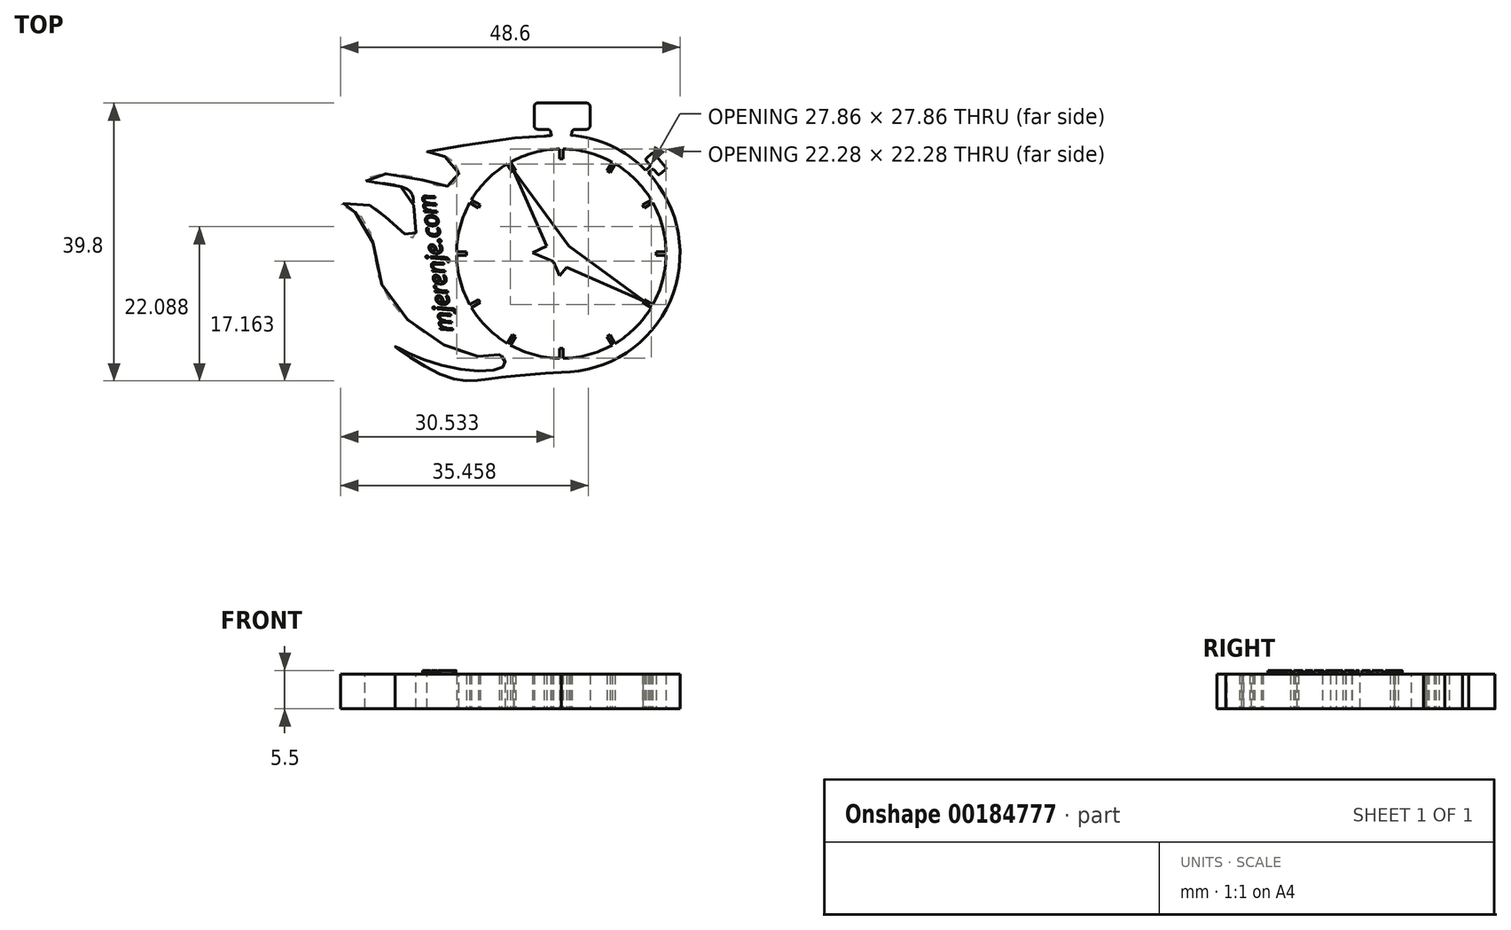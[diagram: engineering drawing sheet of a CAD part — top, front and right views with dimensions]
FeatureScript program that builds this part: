
annotation { "Feature Type Name" : "Feature", "Feature Type Description" : "" }
export const myFeature = defineFeature(function(context is Context, id is Id, definition is map)
    precondition{}
    {
        {
            var Q0;
            Q0=qCreatedBy(makeId("Top.planeOp"),FACE);
            var sketch = newSketch(context, id + "F0", { "sketchPlane" : qUnion([Q0])});
            skArc(sketch, "E0", {"start": v(-0.25, 15) * mm, "mid": v(-3.88, 14.49) * mm, "end": v(-7.28, 13.11) * mm});
            skArc(sketch, "E1.0", {"start": v(-1.33, 16.95) * mm, "mid": v(-1.9, 16.9) * mm, "end": v(-2.47, 16.82) * mm});
            skLineSegment(sketch, "E2.0", {"start": v(-0.25, 15) * mm, "end": v(-0.25, 13.57) * mm});
            skLineSegment(sketch, "E3.0", {"start": v(0.25, 15) * mm, "end": v(0.25, 13.57) * mm});
            skLineSegment(sketch, "E4", {"start": v(-0.25, 13.57) * mm, "end": v(0.25, 13.57) * mm});
            skLineSegment(sketch, "E5", {"start": v(-27.27, 0) * mm, "end": v(32.4, 0) * mm, "construction": true});
            skPoint(sketch, "E6", {"position": v(0, 13.57) * mm});
            skLineSegment(sketch, "E7.1.0", {"start": v(7.28, 13.12) * mm, "end": v(6.57, 11.87) * mm});
            skPoint(sketch, "E7.1.1", {"position": v(6.78, 11.75) * mm});
            skLineSegment(sketch, "E7.1.2", {"start": v(7.72, 12.87) * mm, "end": v(7, 11.62) * mm});
            skLineSegment(sketch, "E7.1.3", {"start": v(6.57, 11.87) * mm, "end": v(7, 11.62) * mm});
            skLineSegment(sketch, "E7.2.0", {"start": v(12.87, 7.72) * mm, "end": v(11.62, 7) * mm});
            skPoint(sketch, "E7.2.1", {"position": v(11.75, 6.78) * mm});
            skLineSegment(sketch, "E7.2.2", {"start": v(13.12, 7.28) * mm, "end": v(11.87, 6.57) * mm});
            skLineSegment(sketch, "E7.2.3", {"start": v(11.62, 7) * mm, "end": v(11.87, 6.57) * mm});
            skLineSegment(sketch, "E7.3.0", {"start": v(15, 0.25) * mm, "end": v(13.57, 0.25) * mm});
            skPoint(sketch, "E7.3.1", {"position": v(13.57, 0) * mm});
            skLineSegment(sketch, "E7.3.2", {"start": v(15, -0.25) * mm, "end": v(13.57, -0.25) * mm});
            skLineSegment(sketch, "E7.3.3", {"start": v(13.57, 0.25) * mm, "end": v(13.57, -0.25) * mm});
            skLineSegment(sketch, "E7.anchor1", {"start": v(0, 0) * mm, "end": v(0, 13.57) * mm, "construction": true});
            skLineSegment(sketch, "E7.anchor2", {"start": v(0, 0) * mm, "end": v(13.57, 0) * mm, "construction": true});
            skLineSegment(sketch, "E8.MirrorCS", {"start": v(-11.62, 7) * mm, "end": v(-11.87, 6.57) * mm});
            skLineSegment(sketch, "E9.MirrorCS", {"start": v(-13.57, 0.25) * mm, "end": v(-13.57, -0.25) * mm});
            skPoint(sketch, "E10.MirrorP", {"position": v(-13.57, 0) * mm});
            skPoint(sketch, "E11.MirrorP", {"position": v(-6.78, 11.75) * mm});
            skLineSegment(sketch, "E12.MirrorCS", {"start": v(-13.12, 7.28) * mm, "end": v(-11.87, 6.57) * mm});
            skLineSegment(sketch, "E13.MirrorCS", {"start": v(-15, 0.25) * mm, "end": v(-13.57, 0.25) * mm});
            skLineSegment(sketch, "E14.MirrorCS", {"start": v(-15, -0.25) * mm, "end": v(-13.57, -0.25) * mm});
            skPoint(sketch, "E15.MirrorP", {"position": v(-11.75, 6.78) * mm});
            skLineSegment(sketch, "E16.MirrorCS", {"start": v(-7.72, 12.87) * mm, "end": v(-7, 11.62) * mm});
            skLineSegment(sketch, "E17.MirrorCS", {"start": v(-12.87, 7.72) * mm, "end": v(-11.62, 7) * mm});
            skLineSegment(sketch, "E18.MirrorCS", {"start": v(-7.28, 13.12) * mm, "end": v(-6.57, 11.87) * mm});
            skLineSegment(sketch, "E19.MirrorCS", {"start": v(-6.57, 11.87) * mm, "end": v(-7, 11.62) * mm});
            skLineSegment(sketch, "E20.MirrorCS", {"start": v(-0.25, -13.57) * mm, "end": v(0.25, -13.57) * mm});
            skLineSegment(sketch, "E21.MirrorCS", {"start": v(6.57, -11.87) * mm, "end": v(7, -11.62) * mm});
            skLineSegment(sketch, "E22.MirrorCS", {"start": v(-11.62, -7) * mm, "end": v(-11.87, -6.57) * mm});
            skLineSegment(sketch, "E23.MirrorCS", {"start": v(-6.57, -11.87) * mm, "end": v(-7, -11.62) * mm});
            skLineSegment(sketch, "E24.MirrorCS", {"start": v(11.62, -7) * mm, "end": v(11.87, -6.57) * mm});
            skLineSegment(sketch, "E25.MirrorCS", {"start": v(-12.87, -7.72) * mm, "end": v(-11.62, -7) * mm});
            skLineSegment(sketch, "E26.MirrorCS", {"start": v(0.25, -15) * mm, "end": v(0.25, -13.57) * mm});
            skLineSegment(sketch, "E27.MirrorCS", {"start": v(-0.25, -15) * mm, "end": v(-0.25, -13.57) * mm});
            skLineSegment(sketch, "E28.MirrorCS", {"start": v(-13.12, -7.28) * mm, "end": v(-11.87, -6.57) * mm});
            skLineSegment(sketch, "E29.MirrorCS", {"start": v(-7.72, -12.87) * mm, "end": v(-7, -11.62) * mm});
            skLineSegment(sketch, "E30.MirrorCS", {"start": v(-7.28, -13.12) * mm, "end": v(-6.57, -11.87) * mm});
            skLineSegment(sketch, "E31.MirrorCS", {"start": v(13.12, -7.28) * mm, "end": v(11.87, -6.57) * mm});
            skLineSegment(sketch, "E32.MirrorCS", {"start": v(7.28, -13.12) * mm, "end": v(6.57, -11.87) * mm});
            skLineSegment(sketch, "E33.MirrorCS", {"start": v(12.87, -7.72) * mm, "end": v(11.62, -7) * mm});
            skLineSegment(sketch, "E34.MirrorCS", {"start": v(7.72, -12.87) * mm, "end": v(7, -11.62) * mm});
            skPoint(sketch, "E35.MirrorP", {"position": v(0, -13.57) * mm});
            skPoint(sketch, "E36.MirrorP", {"position": v(11.75, -6.78) * mm});
            skPoint(sketch, "E37.MirrorP", {"position": v(-11.75, -6.78) * mm});
            skPoint(sketch, "E38.MirrorP", {"position": v(6.78, -11.75) * mm});
            skPoint(sketch, "E39.MirrorP", {"position": v(-6.78, -11.75) * mm});
            skPoint(sketch, "E40.orphan", {"position": v(-0.25, 15) * mm});
            skPoint(sketch, "E41.orphan", {"position": v(0.25, 15) * mm});
            skArc(sketch, "E42.trimOffspring", {"start": v(7.28, 13.11) * mm, "mid": v(3.88, 14.49) * mm, "end": v(0.25, 15) * mm});
            skArc(sketch, "E43.trimOffspring", {"start": v(12.86, 7.72) * mm, "mid": v(10.6, 10.6) * mm, "end": v(7.72, 12.86) * mm});
            skArc(sketch, "E44.trimOffspring", {"start": v(15, 0.25) * mm, "mid": v(14.49, 3.88) * mm, "end": v(13.11, 7.28) * mm});
            skArc(sketch, "E45.trimOffspring", {"start": v(13.11, -7.28) * mm, "mid": v(14.49, -3.88) * mm, "end": v(15, -0.25) * mm});
            skArc(sketch, "E46.trimOffspring", {"start": v(7.72, -12.86) * mm, "mid": v(10.6, -10.6) * mm, "end": v(12.86, -7.72) * mm});
            skArc(sketch, "E47.trimOffspring", {"start": v(0.25, -15) * mm, "mid": v(3.88, -14.49) * mm, "end": v(7.28, -13.11) * mm});
            skArc(sketch, "E48.trimOffspring", {"start": v(-7.28, -13.11) * mm, "mid": v(-3.88, -14.49) * mm, "end": v(-0.25, -15) * mm});
            skArc(sketch, "E49.trimOffspring", {"start": v(-12.86, -7.72) * mm, "mid": v(-10.6, -10.6) * mm, "end": v(-7.72, -12.86) * mm});
            skArc(sketch, "E50.trimOffspring", {"start": v(-15, -0.25) * mm, "mid": v(-14.49, -3.88) * mm, "end": v(-13.11, -7.28) * mm});
            skArc(sketch, "E51.trimOffspring", {"start": v(-13.11, 7.28) * mm, "mid": v(-14.49, 3.88) * mm, "end": v(-15, 0.25) * mm});
            skArc(sketch, "E52.trimOffspring", {"start": v(-7.72, 12.86) * mm, "mid": v(-10.6, 10.6) * mm, "end": v(-12.86, 7.72) * mm});
            skLineSegment(sketch, "E53.0", {"start": v(-1.5, 17.5) * mm, "end": v(-1.5, 17.5) * mm});
            skLineSegment(sketch, "E54.0", {"start": v(-3.39, 17.82) * mm, "end": v(-2, 17.82) * mm});
            skLineSegment(sketch, "E55.0", {"start": v(-3.39, 21.57) * mm, "end": v(0.11, 21.57) * mm});
            skLineSegment(sketch, "E56.0", {"start": v(-3.89, 18.32) * mm, "end": v(-3.89, 21.07) * mm});
            skPoint(sketch, "E57.start.orphan", {"position": v(-4.81, 16.82) * mm});
            skLineSegment(sketch, "E58.MirrorCS", {"start": v(3.61, 21.57) * mm, "end": v(0, 21.57) * mm});
            skLineSegment(sketch, "E59.MirrorCS", {"start": v(4.11, 18.32) * mm, "end": v(4.11, 21.07) * mm});
            skLineSegment(sketch, "E60.MirrorCS", {"start": v(3.61, 17.82) * mm, "end": v(2, 17.82) * mm});
            skLineSegment(sketch, "E61.MirrorCS", {"start": v(1.5, 17.5) * mm, "end": v(1.5, 17.5) * mm});
            skPoint(sketch, "E62.visualSharp", {"position": v(-3.89, 21.57) * mm});
            skArc(sketch, "E62.filletArc", {"start": v(-3.39, 21.57) * mm, "mid": v(-3.74, 21.43) * mm, "end": v(-3.89, 21.07) * mm});
            skPoint(sketch, "E63.visualSharp", {"position": v(-3.89, 17.82) * mm});
            skArc(sketch, "E63.filletArc", {"start": v(-3.89, 18.32) * mm, "mid": v(-3.74, 17.97) * mm, "end": v(-3.39, 17.82) * mm});
            skPoint(sketch, "E64.visualSharp", {"position": v(-1.5, 17.82) * mm});
            skArc(sketch, "E64.filletArc", {"start": v(-1.5, 17.32) * mm, "mid": v(-1.65, 17.67) * mm, "end": v(-2, 17.82) * mm});
            skPoint(sketch, "E65.visualSharp", {"position": v(-1.5, 16.82) * mm});
            skArc(sketch, "E65.filletArc", {"start": v(-1.5, 17.32) * mm, "mid": v(-1.46, 17.12) * mm, "end": v(-1.33, 16.95) * mm});
            skPoint(sketch, "E66.visualSharp", {"position": v(1.5, 16.82) * mm});
            skArc(sketch, "E66.filletArc", {"start": v(1.33, 16.95) * mm, "mid": v(1.46, 17.12) * mm, "end": v(1.5, 17.32) * mm});
            skPoint(sketch, "E67.visualSharp", {"position": v(1.5, 17.82) * mm});
            skArc(sketch, "E67.filletArc", {"start": v(2, 17.82) * mm, "mid": v(1.65, 17.67) * mm, "end": v(1.5, 17.32) * mm});
            skPoint(sketch, "E68.visualSharp", {"position": v(4.11, 17.82) * mm});
            skArc(sketch, "E68.filletArc", {"start": v(3.61, 17.82) * mm, "mid": v(3.97, 17.97) * mm, "end": v(4.11, 18.32) * mm});
            skPoint(sketch, "E69.visualSharp", {"position": v(4.11, 21.57) * mm});
            skArc(sketch, "E69.filletArc", {"start": v(4.11, 21.07) * mm, "mid": v(3.97, 21.43) * mm, "end": v(3.61, 21.57) * mm});
            skPoint(sketch, "E70.trimOffspring.end.orphan", {"position": v(0, 16.82) * mm});
            skLineSegment(sketch, "E71.bottom", {"start": v(13.3, 14.3) * mm, "end": v(14.91, 12.39) * mm});
            skLineSegment(sketch, "E71.top", {"start": v(12.16, 13.34) * mm, "end": v(12.64, 12.76) * mm});
            skLineSegment(sketch, "E71.left", {"start": v(12.95, 14.33) * mm, "end": v(12.19, 13.7) * mm});
            skLineSegment(sketch, "E71.right", {"start": v(14.88, 12.04) * mm, "end": v(14.12, 11.4) * mm});
            skLineSegment(sketch, "E72.top", {"start": v(13.5, 12.53) * mm, "end": v(13.5, 12.53) * mm});
            skLineSegment(sketch, "E72.right", {"start": v(12.93, 12.03) * mm, "end": v(12.42, 11.6) * mm});
            skLineSegment(sketch, "E73.MirrorCS", {"start": v(12.6, 12.41) * mm, "end": v(12.08, 11.97) * mm});
            skPoint(sketch, "E74.newPointA", {"position": v(12.8, 12.57) * mm});
            skPoint(sketch, "E74.newPointB", {"position": v(13.93, 11.23) * mm});
            skArc(sketch, "E74.filletArc", {"start": v(12.6, 12.41) * mm, "mid": v(12.7, 12.58) * mm, "end": v(12.64, 12.76) * mm});
            skPoint(sketch, "E75.visualSharp", {"position": v(12, 13.53) * mm});
            skArc(sketch, "E75.filletArc", {"start": v(12.19, 13.7) * mm, "mid": v(12.1, 13.52) * mm, "end": v(12.16, 13.34) * mm});
            skPoint(sketch, "E76.visualSharp", {"position": v(13.15, 14.5) * mm});
            skArc(sketch, "E76.filletArc", {"start": v(13.3, 14.3) * mm, "mid": v(13.14, 14.4) * mm, "end": v(12.95, 14.33) * mm});
            skPoint(sketch, "E77.visualSharp", {"position": v(15.07, 12.2) * mm});
            skArc(sketch, "E77.filletArc", {"start": v(14.88, 12.04) * mm, "mid": v(14.97, 12.2) * mm, "end": v(14.91, 12.39) * mm});
            skLineSegment(sketch, "E78.MirrorCS", {"start": v(13.76, 11.42) * mm, "end": v(13.28, 12) * mm});
            skArc(sketch, "E79.MirrorCS", {"start": v(14.12, 11.4) * mm, "mid": v(13.93, 11.34) * mm, "end": v(13.76, 11.42) * mm});
            skArc(sketch, "E80.MirrorCS", {"start": v(12.93, 12.03) * mm, "mid": v(13.11, 12.09) * mm, "end": v(13.28, 12) * mm});
            skPoint(sketch, "E72.left.start.orphan", {"position": v(12.96, 12.38) * mm});
            skArc(sketch, "E81.trimOffspring", {"start": v(12.08, 11.97) * mm, "mid": v(7.15, 15.42) * mm, "end": v(1.33, 16.95) * mm});
            skFitSpline(sketch, "E82", {"points": [v(0, -17) * mm, v(-9.93, -17.89) * mm, v(-16.52, -17.6) * mm, v(-23.79, -13.33) * mm, v(-17.78, -15.85) * mm, v(-8.09, -15.95) * mm, v(-8.9, -14.49) * mm, v(-11.3, -14.71) * mm, v(-18.44, -12.13) * mm, v(-25.92, -3.97) * mm, v(-28.42, 5.02) * mm, v(-31.6, 7.03) * mm, v(-28.25, 7.11) * mm, v(-26.4, 6.36) * mm, v(-23.88, 4.09) * mm, v(-21.5, 2.3) * mm, v(-20.9, 2.56) * mm, v(-21.13, 6.39) * mm, v(-22.18, 9.29) * mm, v(-28.1, 10.54) * mm, v(-23.53, 11.47) * mm, v(-17.47, 9.7) * mm, v(-15.33, 10.16) * mm, v(-14.68, 11.84) * mm, v(-17, 14.07) * mm, v(-19.25, 14.53) * mm, v(-9.7, 16.13) * mm, v(-2.47, 16.82) * mm, v(-1.92, 16.4) * mm], "startDerivative": vector(-202.14, -14.42) * mm, "endDerivative": vector(27.1, -35.47) * mm});
            skArc(sketch, "E83.trimOffspring", {"start": v(-8.9, -14.49) * mm, "mid": v(-8.74, -14.58) * mm, "end": v(-8.58, -14.68) * mm});
            skArc(sketch, "E84.trimOffspring", {"start": v(0, -17) * mm, "mid": v(15.6, -6.77) * mm, "end": v(12.42, 11.6) * mm});
            skSolve(sketch);
        }
        {
            var Q0;
            Q0 = qSketchRegion(id + "F0", true);
            extrude(context, id + "F1", {"entities" : qUnion([Q0]), "depth" : 5 * mm});
        }
        {
            var Q0;
            Q0=qCreatedBy(makeId("Top.planeOp"),FACE);
            var sketch = newSketch(context, id + "F2", { "sketchPlane" : qUnion([Q0])});
            skText(sketch, "E85", { "text": "mjerenje.com", "fontName": "OpenSans-Italic.ttf"});
            const initialGuessF2  = {"E85": [-0.01553, -0.01107, -0.13276, 0.99115, 0.0024]};
            skSetInitialGuess(sketch, initialGuessF2);
            skSolve(sketch);
        }
        {
            var Q0;
            Q0 = qSketchRegion(id + "F2", true);
            extrude(context, id + "F3", {"entities" : qUnion([Q0]), "operationType" : NewBodyOperationType.ADD, "depth" : 5.5 * mm});
        }
        {
            var Q0;
            Q0=qCreatedBy(makeId("Top.planeOp"),FACE);
            var sketch = newSketch(context, id + "F4", { "sketchPlane" : qUnion([Q0])});
            skLineSegment(sketch, "E86", {"start": v(-6.93, 12.09) * mm, "end": v(-2.13, 1.11) * mm});
            skLineSegment(sketch, "E87", {"start": v(-6.93, 12.09) * mm, "end": v(1.07, 1.07) * mm});
            skLineSegment(sketch, "E88", {"start": v(0.78, -1.98) * mm, "end": v(-0.26, -3.15) * mm});
            skLineSegment(sketch, "E89", {"start": v(11.95, -6.86) * mm, "end": v(1.07, 1.07) * mm});
            skLineSegment(sketch, "E90", {"start": v(11.95, -6.86) * mm, "end": v(0.78, -1.98) * mm});
            skLineSegment(sketch, "E91", {"start": v(-2.13, 1.11) * mm, "end": v(-4.1, 0.15) * mm});
            skLineSegment(sketch, "E92.trimOffspring", {"start": v(-1.14, -1.14) * mm, "end": v(-0.26, -3.15) * mm});
            skLineSegment(sketch, "E93.trimOffspring", {"start": v(-1.14, -1.14) * mm, "end": v(-4.1, 0.15) * mm});
            skPoint(sketch, "E94.orphan", {"position": v(-4.42, 0) * mm});
            skSolve(sketch);
        }
        {
            var Q0;
            Q0 = qSketchRegion(id + "F4", true);
            extrude(context, id + "F5", {"entities" : qUnion([Q0]), "operationType" : NewBodyOperationType.ADD, "depth" : 5 * mm});
        }
    });
